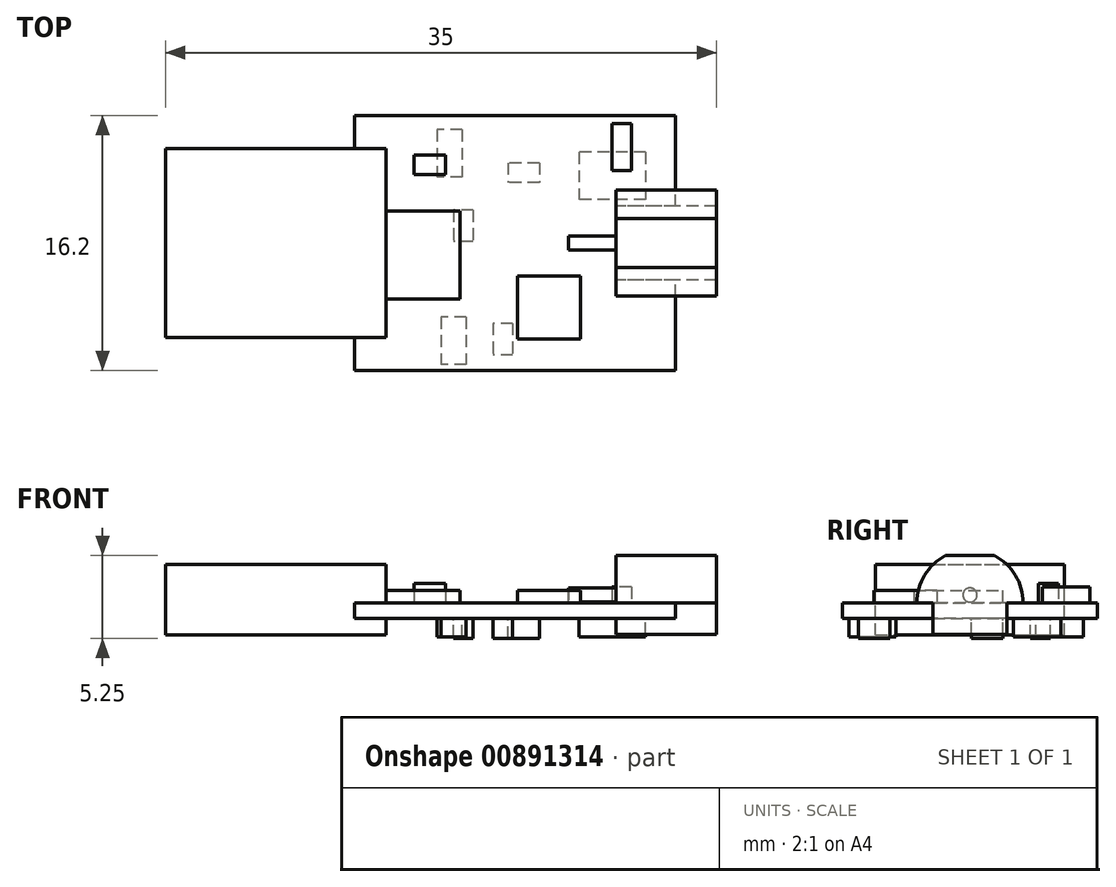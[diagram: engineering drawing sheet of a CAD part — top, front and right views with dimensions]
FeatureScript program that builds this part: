
annotation { "Feature Type Name" : "Feature", "Feature Type Description" : "" }
export const myFeature = defineFeature(function(context is Context, id is Id, definition is map)
    precondition{}
    {
        {
            var Q0;
            Q0=qCreatedBy(makeId("Top.planeOp"),FACE);
            var sketch = newSketch(context, id + "F0", { "sketchPlane" : qUnion([Q0])});
            skLineSegment(sketch, "E0.bottom", {"start": v(10.2, -8.1) * mm, "end": v(-10.2, -8.1) * mm});
            skLineSegment(sketch, "E0.top", {"start": v(10.2, 8.1) * mm, "end": v(-10.2, 8.1) * mm});
            skLineSegment(sketch, "E0.left", {"start": v(10.2, -8.1) * mm, "end": v(10.2, 8.1) * mm});
            skLineSegment(sketch, "E0.right", {"start": v(-10.2, -8.1) * mm, "end": v(-10.2, 8.1) * mm});
            skPoint(sketch, "E0.middle", {"position": v(0, 0) * mm});
            skSolve(sketch);
        }
        {
            var Q0;
            Q0=makeQuery(id+"F0.imprint","IMPRINT",FACE,{"disambiguationData":[TD([[makeQuery(id+"F0.imprint","IMPRINT",EDGE,{"derivedFrom":sQuery(id+"F0.wireOp",EDGE,"E0.bottom")}),-1.0]])]});
            extrude(context, id + "F1", {"entities" : qUnion([Q0]), "oppositeDirection" : true, "depth" : 1 * mm});
        }
        {
            var Q0;
            Q0=makeQuery(id+"F1.opExtrude","SWEPT_FACE",FACE,{"disambiguationData":[OSD([sQuery(id+"F0.wireOp",EDGE,"E0.right")])]});
            var sketch = newSketch(context, id + "F2", { "sketchPlane" : qUnion([Q0])});
            skLineSegment(sketch, "E1.bottom", {"start": v(6, -2.05) * mm, "end": v(-6, -2.05) * mm});
            skLineSegment(sketch, "E1.top", {"start": v(6, 2.45) * mm, "end": v(-6, 2.45) * mm});
            skLineSegment(sketch, "E1.left", {"start": v(6, -2.05) * mm, "end": v(6, 2.45) * mm});
            skLineSegment(sketch, "E1.right", {"start": v(-6, -2.05) * mm, "end": v(-6, 2.45) * mm});
            skPoint(sketch, "E1.middle", {"position": v(0, 0.2) * mm});
            skSolve(sketch);
        }
        {
            var Q0;
            Q0=qSketchRegion(id+"F2",true);
            extrude(context, id + "F3", {"entities" : qUnion([Q0]), "operationType" : NewBodyOperationType.ADD, "depth" : 12 * mm, "hasSecondDirection" : true, "secondDirectionOppositeDirection" : true, "secondDirectionDepth" : 2 * mm});
        }
        {
            var Q0;
            Q0=makeQuery(id+"F1.opExtrude","SWEPT_FACE",FACE,{"disambiguationData":[OSD([sQuery(id+"F0.wireOp",EDGE,"E0.left")])]});
            var sketch = newSketch(context, id + "F4", { "sketchPlane" : qUnion([Q0])});
            skLineSegment(sketch, "E2.top", {"start": v(-2.35, -2) * mm, "end": v(2.35, -2) * mm});
            skLineSegment(sketch, "E2.left", {"start": v(-2.35, 0) * mm, "end": v(-2.35, -2) * mm});
            skLineSegment(sketch, "E2.right", {"start": v(2.35, 0) * mm, "end": v(2.35, -2) * mm});
            skLineSegment(sketch, "E3", {"start": v(0, 0) * mm, "end": v(0, 1.3) * mm, "construction": true});
            skPoint(sketch, "E3.endSnap0", {"position": v(0, 0) * mm});
            skLineSegment(sketch, "E4", {"start": v(-2.35, 0) * mm, "end": v(-3.37, 0) * mm});
            skLineSegment(sketch, "E5", {"start": v(2.35, 0) * mm, "end": v(3.38, 0) * mm});
            skArc(sketch, "E6", {"start": v(3.38, 0) * mm, "mid": v(2.88, 1.76) * mm, "end": v(1.55, 3) * mm});
            skLineSegment(sketch, "E7", {"start": v(-1.55, 3) * mm, "end": v(1.55, 3) * mm});
            skArc(sketch, "E8.trimOffspring", {"start": v(-1.55, 3) * mm, "mid": v(-2.88, 1.76) * mm, "end": v(-3.37, 0) * mm});
            skSolve(sketch);
        }
        {
            var Q0;
            {var subQ0=sQuery(id+"F4.wireOp",EDGE,"E2.top");Q0=makeQuery(id+"F4.imprint","IMPRINT",FACE,{"disambiguationData":[TD([[makeQuery(id+"F4.imprint","IMPRINT",EDGE,{"derivedFrom":subQ0}),1.0]])]});}
            var Q1;
            {var subQ0=sQuery(id+"F4.wireOp",EDGE,"E2.left");var subQ1=sQuery(id+"F0.wireOp",EDGE,"E0.left");var subQ4=makeQuery(id+"F1.opExtrude","CAP_EDGE",EDGE,{"disambiguationData":[OSD([subQ1])],"isStart":false});var subQ5=makeQuery(id+"F4.imprint","INTERSECT",VERTEX,{"derivedFrom":[subQ4,subQ0]});Q1=makeQuery(id+"F4.imprint","IMPRINT",FACE,{"disambiguationData":[TD([[makeQuery(id+"F4.imprint","IMPRINT",EDGE,{"disambiguationData":[TD([[subQ5,-1.0]])],"derivedFrom":subQ4}),1.0]])]});}
            var Q2;
            {var subQ1=sQuery(id+"F4.wireOp",EDGE,"E4");Q2=makeQuery(id+"F4.imprint","IMPRINT",FACE,{"disambiguationData":[TD([[makeQuery(id+"F4.imprint","IMPRINT",EDGE,{"derivedFrom":subQ1}),1.0]])]});}
            extrude(context, id + "F5", {"entities" : qUnion([Q0, Q1, Q2]), "operationType" : NewBodyOperationType.ADD, "depth" : 2.6 * mm, "hasSecondDirection" : true, "secondDirectionOppositeDirection" : true, "secondDirectionDepth" : (6.4 - 2.6) * mm});
        }
        {
            var Q0;
            {var subQ0=sQuery(id+"F4.wireOp",EDGE,"E6");var subQ1=sQuery(id+"F4.wireOp",EDGE,"E7");var subQ2=sQuery(id+"F4.wireOp",EDGE,"E8.trimOffspring");Q0=makeQuery(id+"F5.boolean.opBoolean","SPLIT",FACE,{"disambiguationData":[TD([makeQuery(id+"F5.opExtrude","SWEPT_FACE",FACE,{"disambiguationData":[OSD([subQ0])]})])],"derivedFrom":makeQuery(id+"F5.opExtrude","CAP_FACE",FACE,{"disambiguationData":[OSD([sQuery(id+"F4.wireOp",EDGE,"E2.top"),sQuery(id+"F4.wireOp",EDGE,"E2.left"),sQuery(id+"F4.wireOp",EDGE,"E2.right"),sQuery(id+"F4.wireOp",EDGE,"E4"),sQuery(id+"F4.wireOp",EDGE,"E5"),subQ0,subQ1,subQ2])],"isStart":true})});}
            var sketch = newSketch(context, id + "F6", { "sketchPlane" : qUnion([Q0])});
            skCircle(sketch, "E9", {"center": v(0, 0.5) * mm, "radius": 0.45 * mm});
            skLineSegment(sketch, "E10.0.0", {"start": v(2.35, 0) * mm, "end": v(2.35, -2) * mm, "construction": true});
            skLineSegment(sketch, "E10.0.1", {"start": v(2.35, -2) * mm, "end": v(-2.35, -2) * mm, "construction": true});
            skLineSegment(sketch, "E10.0.2", {"start": v(-2.35, -2) * mm, "end": v(-2.35, 0) * mm, "construction": true});
            skLineSegment(sketch, "E10.0.3", {"start": v(-2.35, 0) * mm, "end": v(-3.38, 0) * mm, "construction": true});
            skArc(sketch, "E10.0.4", {"start": v(-3.38, 0) * mm, "mid": v(-2.88, 1.76) * mm, "end": v(-1.55, 3) * mm, "construction": true});
            skLineSegment(sketch, "E10.0.5", {"start": v(-1.55, 3) * mm, "end": v(1.55, 3) * mm, "construction": true});
            skArc(sketch, "E10.0.6", {"start": v(1.55, 3) * mm, "mid": v(2.88, 1.76) * mm, "end": v(3.37, 0) * mm, "construction": true});
            skLineSegment(sketch, "E10.0.7", {"start": v(3.37, 0) * mm, "end": v(2.35, 0) * mm, "construction": true});
            skCircle(sketch, "E11", {"center": v(0, 0.5) * mm, "radius": 1.73 * mm, "construction": true});
            skLineSegment(sketch, "E12", {"start": v(2.4, 0.5) * mm, "end": v(-2.45, 0.5) * mm, "construction": true});
            skSolve(sketch);
        }
        {
            var Q0;
            Q0=qSketchRegion(id+"F6",true);
            extrude(context, id + "F7", {"entities" : qUnion([Q0]), "operationType" : NewBodyOperationType.ADD, "depth" : 3 * mm});
        }
        {
            var Q0;
            Q0=makeQuery(id+"F1.opExtrude","CAP_FACE",FACE,{"disambiguationData":[OSD([sQuery(id+"F0.wireOp",EDGE,"E0.bottom"),sQuery(id+"F0.wireOp",EDGE,"E0.top"),sQuery(id+"F0.wireOp",EDGE,"E0.left"),sQuery(id+"F0.wireOp",EDGE,"E0.right")])],"isStart":true});
            var sketch = newSketch(context, id + "F8", { "sketchPlane" : qUnion([Q0])});
            skLineSegment(sketch, "E13.bottom", {"start": v(-9.1, 2.05) * mm, "end": v(-3.5, 2.05) * mm});
            skLineSegment(sketch, "E13.top", {"start": v(-9.1, -3.55) * mm, "end": v(-3.5, -3.55) * mm});
            skLineSegment(sketch, "E13.left", {"start": v(-9.1, 2.05) * mm, "end": v(-9.1, -3.55) * mm});
            skLineSegment(sketch, "E13.right", {"start": v(-3.5, 2.05) * mm, "end": v(-3.5, -3.55) * mm});
            skSolve(sketch);
        }
        {
            var Q0;
            Q0=qSketchRegion(id+"F8",true);
            extrude(context, id + "F9", {"entities" : qUnion([Q0]), "operationType" : NewBodyOperationType.ADD, "depth" : .8 * mm});
        }
        {
            var Q0;
            Q0=makeQuery(id+"F1.opExtrude","CAP_FACE",FACE,{"disambiguationData":[OSD([sQuery(id+"F0.wireOp",EDGE,"E0.bottom"),sQuery(id+"F0.wireOp",EDGE,"E0.top"),sQuery(id+"F0.wireOp",EDGE,"E0.left"),sQuery(id+"F0.wireOp",EDGE,"E0.right")])],"isStart":true});
            var sketch = newSketch(context, id + "F10", { "sketchPlane" : qUnion([Q0])});
            skLineSegment(sketch, "E14.bottom", {"start": v(0.15, -2.1) * mm, "end": v(4.15, -2.1) * mm});
            skLineSegment(sketch, "E14.top", {"start": v(0.15, -6.1) * mm, "end": v(4.15, -6.1) * mm});
            skLineSegment(sketch, "E14.left", {"start": v(0.15, -2.1) * mm, "end": v(0.15, -6.1) * mm});
            skLineSegment(sketch, "E14.right", {"start": v(4.15, -2.1) * mm, "end": v(4.15, -6.1) * mm});
            skSolve(sketch);
        }
        {
            var Q0;
            Q0=qSketchRegion(id+"F10",true);
            extrude(context, id + "F11", {"entities" : qUnion([Q0]), "operationType" : NewBodyOperationType.ADD, "depth" : .8 * mm});
        }
        {
            var Q0;
            Q0=makeQuery(id+"F1.opExtrude","CAP_FACE",FACE,{"disambiguationData":[OSD([sQuery(id+"F0.wireOp",EDGE,"E0.bottom"),sQuery(id+"F0.wireOp",EDGE,"E0.top"),sQuery(id+"F0.wireOp",EDGE,"E0.left"),sQuery(id+"F0.wireOp",EDGE,"E0.right")])],"isStart":true});
            var sketch = newSketch(context, id + "F12", { "sketchPlane" : qUnion([Q0])});
            skLineSegment(sketch, "E15.bottom", {"start": v(-6.4, 5.6) * mm, "end": v(-4.4, 5.6) * mm});
            skLineSegment(sketch, "E15.top", {"start": v(-6.4, 4.35) * mm, "end": v(-4.4, 4.35) * mm});
            skLineSegment(sketch, "E15.left", {"start": v(-6.4, 5.6) * mm, "end": v(-6.4, 4.35) * mm});
            skLineSegment(sketch, "E15.right", {"start": v(-4.4, 5.6) * mm, "end": v(-4.4, 4.35) * mm});
            skSolve(sketch);
        }
        {
            var Q0;
            Q0=qSketchRegion(id+"F12",true);
            extrude(context, id + "F13", {"entities" : qUnion([Q0]), "operationType" : NewBodyOperationType.ADD, "depth" : 1.25 * mm});
        }
        {
            var Q0;
            Q0=makeQuery(id+"F12.imprint","IMPRINT",FACE,{"disambiguationData":[TD([[makeQuery(id+"F12.imprint","IMPRINT",EDGE,{"derivedFrom":sQuery(id+"F12.wireOp",EDGE,"E15.bottom")}),1.0]])]});
            var sketch = newSketch(context, id + "F14", { "sketchPlane" : qUnion([Q0])});
            skLineSegment(sketch, "E16.bottom", {"start": v(7.4, 4.6) * mm, "end": v(6.15, 4.6) * mm});
            skLineSegment(sketch, "E16.top", {"start": v(7.4, 7.6) * mm, "end": v(6.15, 7.6) * mm});
            skLineSegment(sketch, "E16.left", {"start": v(7.4, 4.6) * mm, "end": v(7.4, 7.6) * mm});
            skLineSegment(sketch, "E16.right", {"start": v(6.15, 4.6) * mm, "end": v(6.15, 7.6) * mm});
            skSolve(sketch);
        }
        {
            var Q0;
            Q0=qSketchRegion(id+"F14",true);
            extrude(context, id + "F15", {"entities" : qUnion([Q0]), "operationType" : NewBodyOperationType.ADD, "depth" : 1 * mm});
        }
        {
            var Q0;
            Q0=makeQuery(id+"F1.opExtrude","CAP_FACE",FACE,{"disambiguationData":[OSD([sQuery(id+"F0.wireOp",EDGE,"E0.bottom"),sQuery(id+"F0.wireOp",EDGE,"E0.top"),sQuery(id+"F0.wireOp",EDGE,"E0.left"),sQuery(id+"F0.wireOp",EDGE,"E0.right")])],"isStart":false});
            var sketch = newSketch(context, id + "F16", { "sketchPlane" : qUnion([Q0])});
            skLineSegment(sketch, "E17.bottom", {"start": v(1.55, -5.1) * mm, "end": v(-0.45, -5.1) * mm});
            skLineSegment(sketch, "E17.top", {"start": v(1.55, -3.85) * mm, "end": v(-0.45, -3.85) * mm});
            skLineSegment(sketch, "E17.left", {"start": v(1.55, -5.1) * mm, "end": v(1.55, -3.85) * mm});
            skLineSegment(sketch, "E17.right", {"start": v(-0.45, -5.1) * mm, "end": v(-0.45, -3.85) * mm});
            skLineSegment(sketch, "E18.bottom", {"start": v(-2.65, -2.1) * mm, "end": v(-3.9, -2.1) * mm});
            skLineSegment(sketch, "E18.top", {"start": v(-2.65, -0.1) * mm, "end": v(-3.9, -0.1) * mm});
            skLineSegment(sketch, "E18.left", {"start": v(-2.65, -2.1) * mm, "end": v(-2.65, -0.1) * mm});
            skLineSegment(sketch, "E18.right", {"start": v(-3.9, -2.1) * mm, "end": v(-3.9, -0.1) * mm});
            skLineSegment(sketch, "E19.bottom", {"start": v(-0.15, 5.1) * mm, "end": v(-1.4, 5.1) * mm});
            skLineSegment(sketch, "E19.top", {"start": v(-0.15, 7.1) * mm, "end": v(-1.4, 7.1) * mm});
            skLineSegment(sketch, "E19.left", {"start": v(-0.15, 5.1) * mm, "end": v(-0.15, 7.1) * mm});
            skLineSegment(sketch, "E19.right", {"start": v(-1.4, 5.1) * mm, "end": v(-1.4, 7.1) * mm});
            skSolve(sketch);
        }
        {
            var Q0;
            Q0=qSketchRegion(id+"F16",true);
            extrude(context, id + "F17", {"entities" : qUnion([Q0]), "operationType" : NewBodyOperationType.ADD, "depth" : 1.25 * mm});
        }
        {
            var Q0;
            Q0=makeQuery(id+"F1.opExtrude","CAP_FACE",FACE,{"disambiguationData":[OSD([sQuery(id+"F0.wireOp",EDGE,"E0.bottom"),sQuery(id+"F0.wireOp",EDGE,"E0.top"),sQuery(id+"F0.wireOp",EDGE,"E0.left"),sQuery(id+"F0.wireOp",EDGE,"E0.right")])],"isStart":false});
            var sketch = newSketch(context, id + "F18", { "sketchPlane" : qUnion([Q0])});
            skLineSegment(sketch, "E20.bottom", {"start": v(-3.35, -7.2) * mm, "end": v(-4.95, -7.2) * mm});
            skLineSegment(sketch, "E20.top", {"start": v(-3.35, -4.2) * mm, "end": v(-4.95, -4.2) * mm});
            skLineSegment(sketch, "E20.left", {"start": v(-3.35, -7.2) * mm, "end": v(-3.35, -4.2) * mm});
            skLineSegment(sketch, "E20.right", {"start": v(-4.95, -7.2) * mm, "end": v(-4.95, -4.2) * mm});
            skLineSegment(sketch, "E21.bottom", {"start": v(-3.1, 4.7) * mm, "end": v(-4.7, 4.7) * mm});
            skLineSegment(sketch, "E21.top", {"start": v(-3.1, 7.7) * mm, "end": v(-4.7, 7.7) * mm});
            skLineSegment(sketch, "E21.left", {"start": v(-3.1, 4.7) * mm, "end": v(-3.1, 7.7) * mm});
            skLineSegment(sketch, "E21.right", {"start": v(-4.7, 4.7) * mm, "end": v(-4.7, 7.7) * mm});
            skSolve(sketch);
        }
        {
            var Q0;
            Q0=qSketchRegion(id+"F18",true);
            extrude(context, id + "F19", {"entities" : qUnion([Q0]), "operationType" : NewBodyOperationType.ADD, "depth" : 1.15 * mm});
        }
        {
            var Q0;
            Q0=makeQuery(id+"F1.opExtrude","CAP_FACE",FACE,{"disambiguationData":[OSD([sQuery(id+"F0.wireOp",EDGE,"E0.bottom"),sQuery(id+"F0.wireOp",EDGE,"E0.top"),sQuery(id+"F0.wireOp",EDGE,"E0.left"),sQuery(id+"F0.wireOp",EDGE,"E0.right")])],"isStart":false});
            var sketch = newSketch(context, id + "F20", { "sketchPlane" : qUnion([Q0])});
            skLineSegment(sketch, "E22.bottom", {"start": v(8.3, -5.77) * mm, "end": v(4.05, -5.77) * mm});
            skLineSegment(sketch, "E22.top", {"start": v(8.3, -2.77) * mm, "end": v(4.05, -2.77) * mm});
            skLineSegment(sketch, "E22.left", {"start": v(8.3, -5.77) * mm, "end": v(8.3, -2.77) * mm});
            skLineSegment(sketch, "E22.right", {"start": v(4.05, -5.77) * mm, "end": v(4.05, -2.77) * mm});
            skSolve(sketch);
        }
        {
            var Q0;
            Q0=qSketchRegion(id+"F20",true);
            extrude(context, id + "F21", {"entities" : qUnion([Q0]), "operationType" : NewBodyOperationType.ADD, "depth" : 1.15 * mm});
        }
    });
